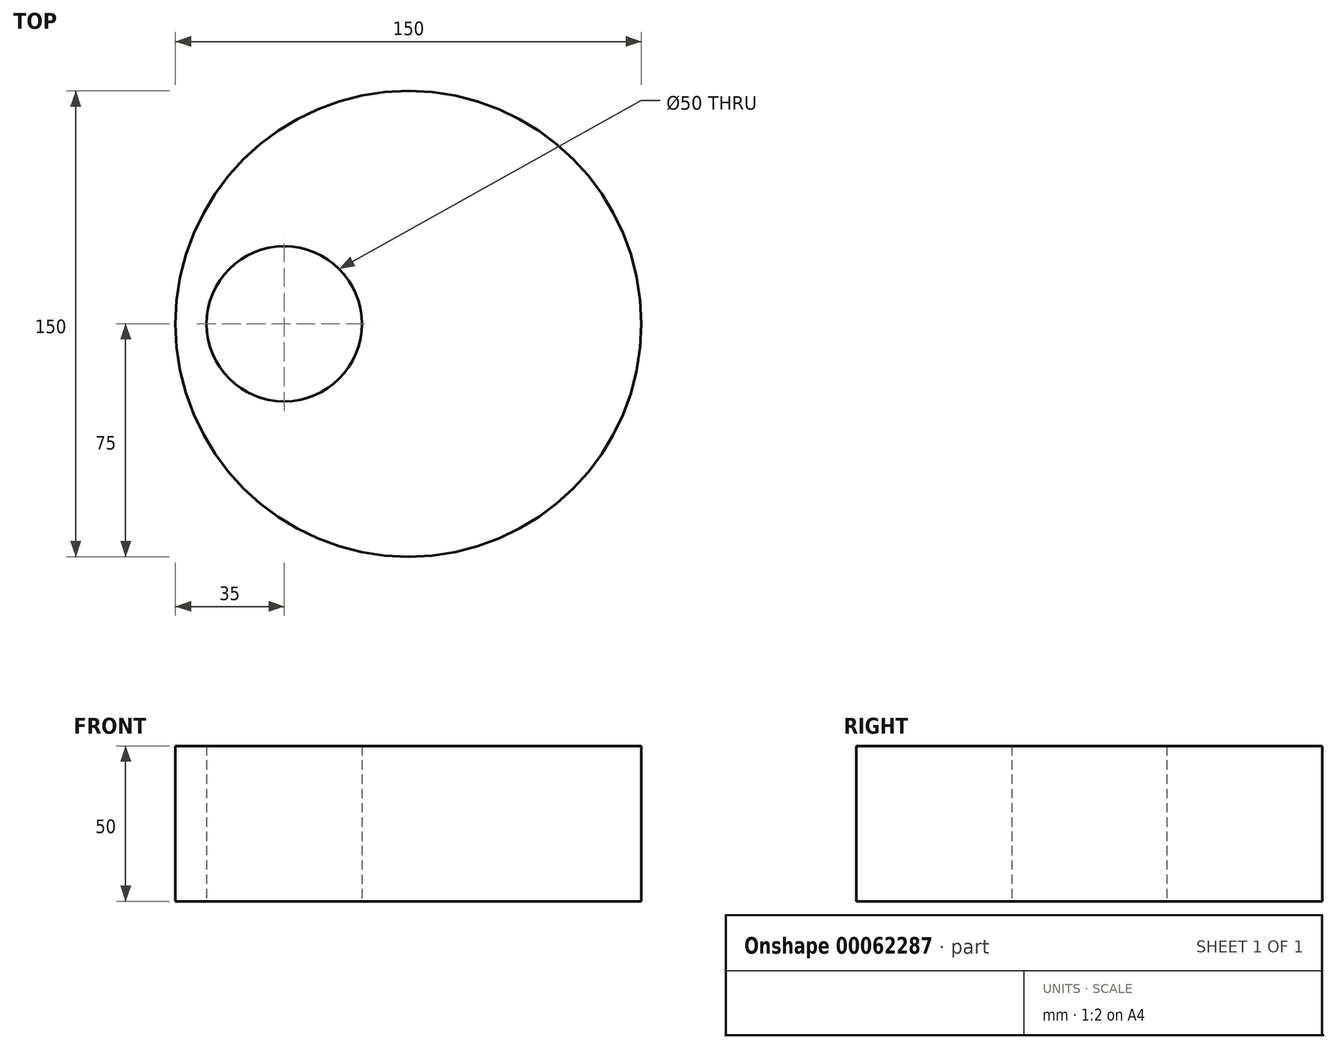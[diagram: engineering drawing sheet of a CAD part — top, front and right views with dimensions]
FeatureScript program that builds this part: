
annotation { "Feature Type Name" : "Feature", "Feature Type Description" : "" }
export const myFeature = defineFeature(function(context is Context, id is Id, definition is map)
    precondition{}
    {
        {
            var Q0;
            Q0=qCreatedBy(makeId("Top.planeOp"),FACE);
            var sketch = newSketch(context, id + "F1", { "sketchPlane" : qUnion([Q0])});
            skCircle(sketch, "E0", {"center": v(0, 0) * mm, "radius": 25 * mm});
            skCircle(sketch, "E1", {"center": v(40, 0) * mm, "radius": 75 * mm});
            skSolve(sketch);
        }
        {
            var Q0;
            Q0 = qSketchRegion(id + "F1", true);
            extrude(context, id + "F0", {"entities" : qUnion([Q0]), "depth" : 50 * mm});
        }
    });
